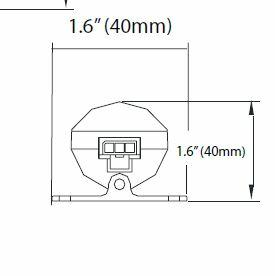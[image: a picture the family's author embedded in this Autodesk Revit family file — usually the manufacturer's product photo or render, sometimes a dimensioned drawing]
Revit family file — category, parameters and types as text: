
# Revit family: Lighting-Surface-Acclaim-Flex Graze HO SC
name_source: partatom
category: Lighting Fixtures
units: mm (PartAtom-declared; Revit-internal decimal feet)

## family parameters
Cut with Voids When Loaded = No
Host = Face
Light Source = Yes
Part Type = Normal
Room Calculation Point = No
Round Connector Dimension = Use Diameter
Shared = No

## types (1)
- Lighting-Surface-Acclaim-Flex Graze HO SC
    Apparent Load = 0 VA
    Color Filter = 16777215
    Default Elevation = 48 "
    Description = Linear LED Strip
    Dimming Lamp Color Temperature Shift = <None>
    Emit from Line Length = 24 "
    Height = 0.98 "
    Housing Finish = Aluminum
    Lamp = LED
    Length = 24 "
    Manufacturer = Acclaim Lighting
    Model = Flex Graze HO SC
    Number of Poles = 1
    Photometric Web File = Load File
    Power Factor = 1
    Tilt Angle = 90.00°
    URL = http://www.acclaimlighting.com
    Voltage = 0 V
    Width = 1.38 "

## geometry (parser evidence)
native form markers: Blend x13, Sweep x3
no freeform markers — native parametric forms only
